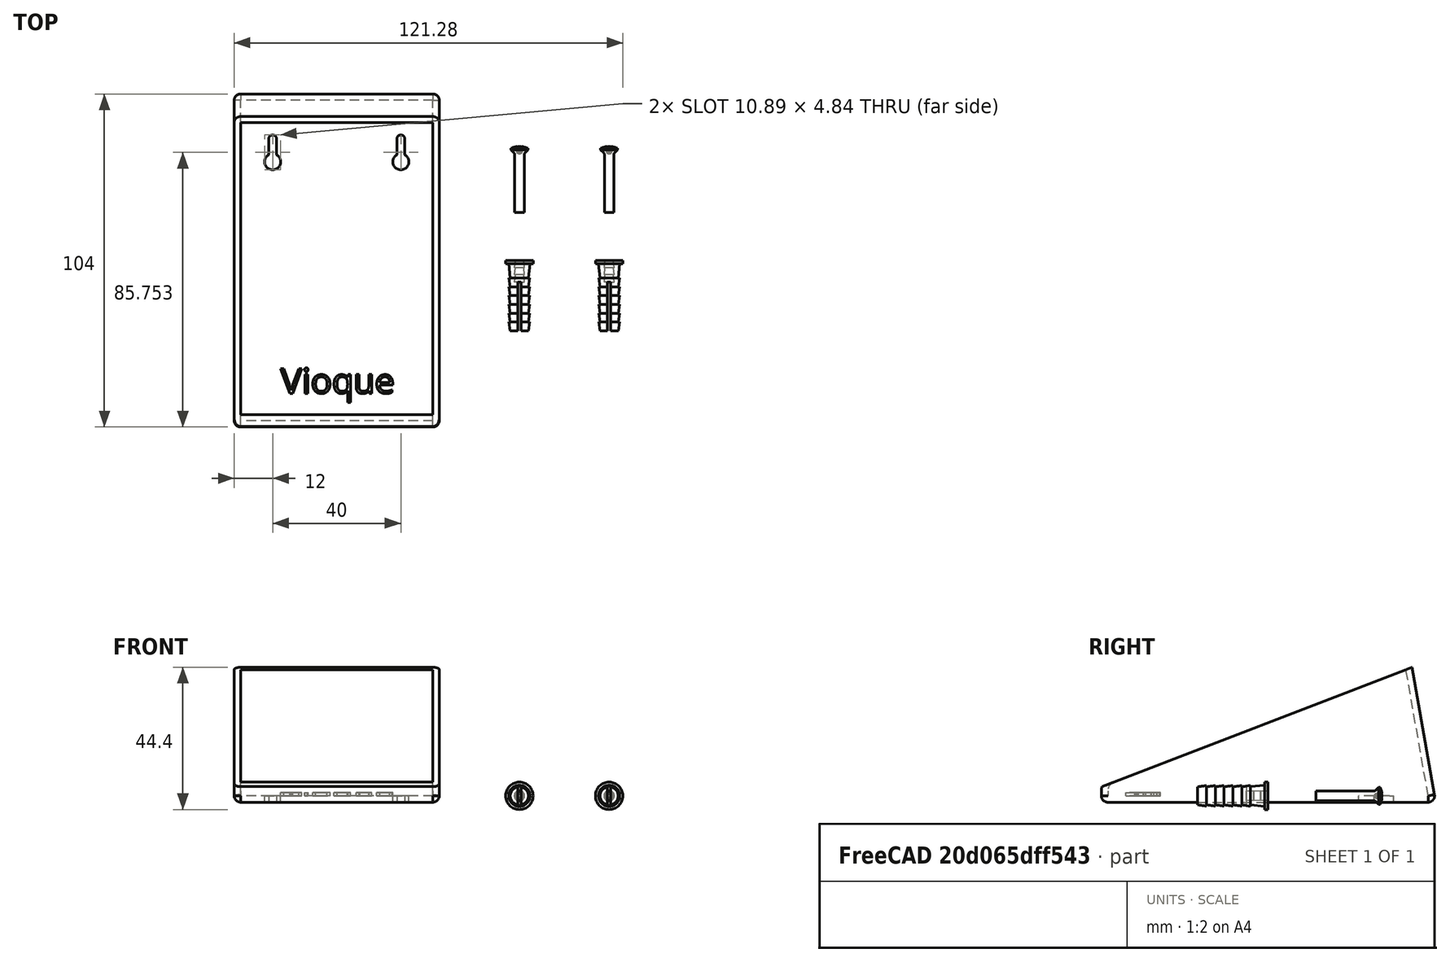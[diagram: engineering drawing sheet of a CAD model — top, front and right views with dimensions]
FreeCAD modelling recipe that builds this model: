
FCSTD DOCUMENT  (FreeCAD 0.16R6703 (Git))
Label: Cubre-timbres-boom
License: CreativeCommons Attribution-ShareAlike
LicenseURL: http://creativecommons.org/licenses/by-sa/4.0/
objects: Part::Feature×5, App::Annotation×3, Part::Part2DObjectPython×3, App::DocumentObjectGroup×1
note: 8 computed .brp shape members not serialized (recipe doc carries the construction recipe); baked Part::Feature solids carry a one-line shape summary decoded from their .brp

FEATURE [Part::Feature] Compound001
  Placement = pos=(-15,0,0) rot=(0,0,-1;1.5708rad)
  shape: bbox 64 x 104.4 x 42.13 mm, 142 faces (baked)
FEATURE [Part::Feature] Common001
  Placement = pos=(12,0,0) rot=(-1,0,0;1.5708rad)
  shape: bbox 8.56 x 21.95 x 8.56 mm, 44 faces (baked)
FEATURE [Part::Feature] Common002
  Placement = pos=(40,0,0) rot=(-1,0,0;1.5708rad)
  shape: bbox 8.56 x 21.95 x 8.56 mm, 44 faces (baked)
FEATURE [App::Annotation] Text
  LabelText = TACOS NYLON
  Position = (11,-30,0)
FEATURE [App::Annotation] Text001
  LabelText = CUBRE TIMBRES
  Position = (-62,-59,0)
FEATURE [Part::Part2DObjectPython] Line001  # Draft 2D object (typed FeaturePython)
  ChamferSize = 0
  Closed = false
  End = (56,-63,0)
  FilletRadius = 0
  Length = 126
  MakeFace = true
  Points = (2) [(56,63,0),(56,-63,0)]
  Start = (56,63,0)
  Subdivisions = 0
FEATURE [Part::Part2DObjectPython] DWire  # Draft 2D object (typed FeaturePython)
  ChamferSize = 0
  Closed = false
  End = (-90,63,0)
  FilletRadius = 0
  Length = 272
  MakeFace = true
  Points = (3) [(56,-63,0),(-90,-63,0),(-90,63,0)]
  Start = (56,-63,0)
  Subdivisions = 0
FEATURE [Part::Part2DObjectPython] Line  # Draft 2D object (typed FeaturePython)
  ChamferSize = 0
  Closed = false
  End = (56,63,0)
  FilletRadius = 0
  Length = 146
  MakeFace = true
  Points = (2) [(-90,63,0),(56,63,0)]
  Start = (-90,63,0)
  Subdivisions = 0
FEATURE [App::Annotation] Text002
  LabelText = TORNILLOS PARED
  Position = (7,7,0)
FEATURE [Part::Feature] Part__Feature001  label="ISO7047-M3x20_"
  Placement = pos=(12,35,0) rot=(-1,0,0;1.5708rad)
  shape: bbox 5.3 x 20.57 x 5.3 mm, 27 faces (baked)
FEATURE [Part::Feature] Part__Feature002  label="ISO7047-M3x20_001"
  Placement = pos=(40,35,0) rot=(-1,0,0;1.5708rad)
  shape: bbox 5.3 x 20.57 x 5.3 mm, 27 faces (baked)
FEATURE [App::DocumentObjectGroup] Group  label="Parts"
  Group = -> [Part__Feature002,Part__Feature001,Common002,Common001,Compound001]
